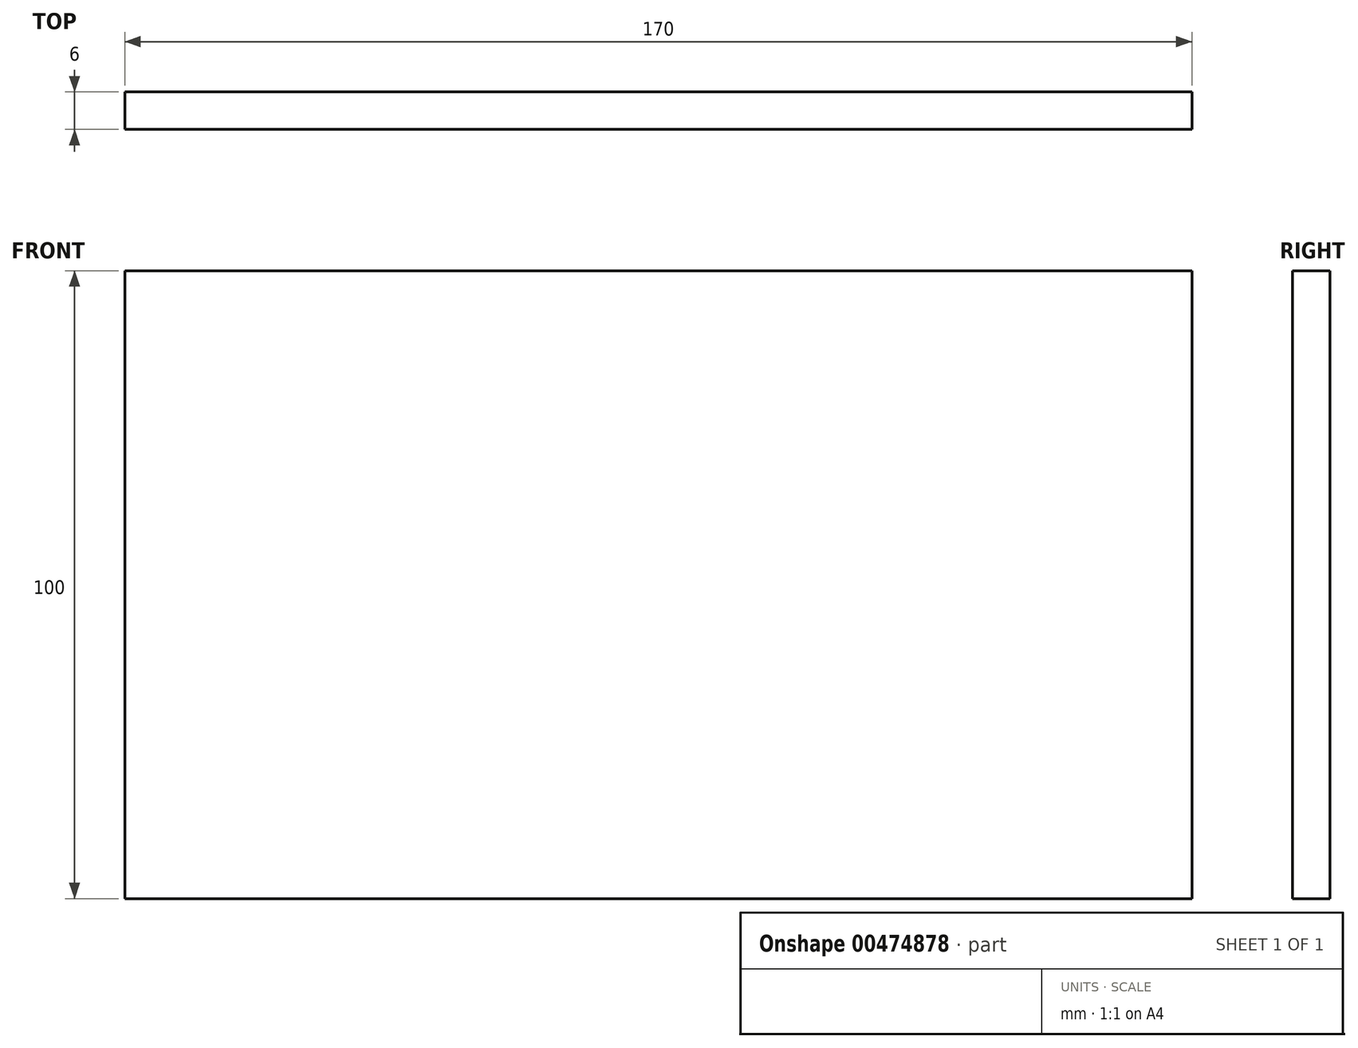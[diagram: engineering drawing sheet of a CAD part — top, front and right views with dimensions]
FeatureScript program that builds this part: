
annotation { "Feature Type Name" : "Feature", "Feature Type Description" : "" }
export const myFeature = defineFeature(function(context is Context, id is Id, definition is map)
    precondition{}
    {
        {
            var Q0;
            Q0=qCreatedBy(makeId("Front.planeOp"),FACE);
            var sketch = newSketch(context, id + "F0", { "sketchPlane" : qUnion([Q0])});
            skLineSegment(sketch, "E0.bottom", {"start": v(85, -50) * mm, "end": v(-85, -50) * mm});
            skLineSegment(sketch, "E0.top", {"start": v(85, 50) * mm, "end": v(-85, 50) * mm});
            skLineSegment(sketch, "E0.left", {"start": v(85, -50) * mm, "end": v(85, 50) * mm});
            skLineSegment(sketch, "E0.right", {"start": v(-85, -50) * mm, "end": v(-85, 50) * mm});
            skPoint(sketch, "E0.middle", {"position": v(0, 0) * mm});
            skSolve(sketch);
        }
        {
            var Q0;
            Q0 = qSketchRegion(id + "F0", true);
            extrude(context, id + "F1", {"entities" : qUnion([Q0]), "endBound" : BoundingType.SYMMETRIC, "depth" : 6 * mm});
        }
    });
